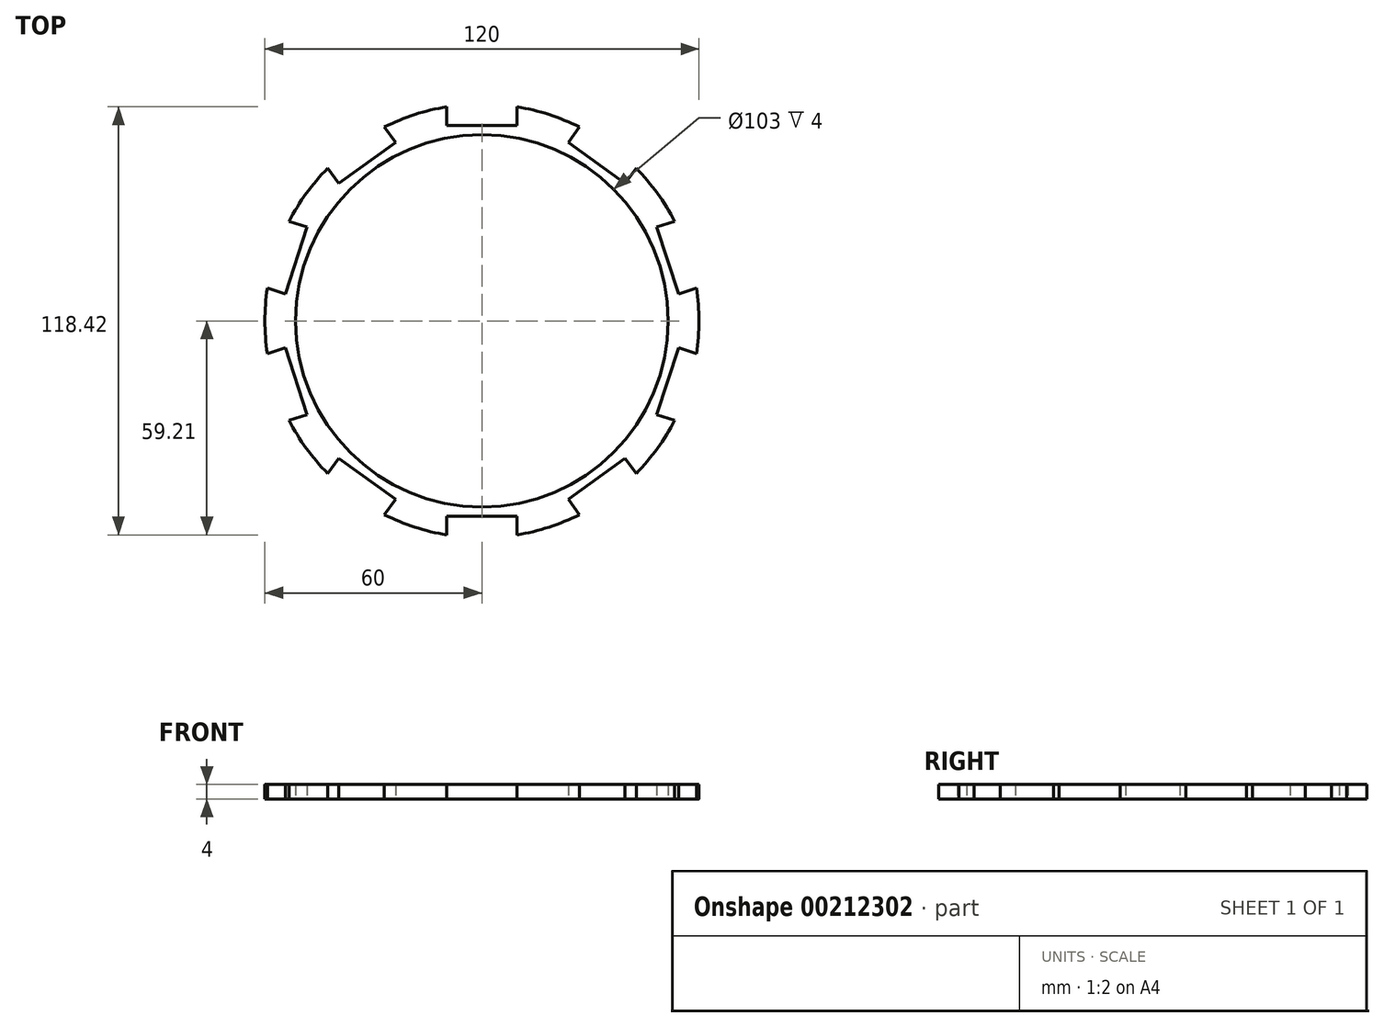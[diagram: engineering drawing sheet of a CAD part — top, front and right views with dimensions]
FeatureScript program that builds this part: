
annotation { "Feature Type Name" : "Feature", "Feature Type Description" : "" }
export const myFeature = defineFeature(function(context is Context, id is Id, definition is map)
    precondition{}
    {
        {
            var Q0;
            Q0=qCreatedBy(makeId("Top.planeOp"),FACE);
            var sketch = newSketch(context, id + "F0", { "sketchPlane" : qUnion([Q0])});
            skCircle(sketch, "E0", {"center": v(0, 0) * mm, "radius": 50 * mm});
            skLineSegment(sketch, "E1", {"start": v(0, 0) * mm, "end": v(0, -93.47) * mm, "construction": true});
            skPoint(sketch, "E2", {"position": v(0, -54) * mm});
            skPoint(sketch, "E3", {"position": v(0, -50) * mm});
            skLineSegment(sketch, "E4.bottom", {"start": v(9.7, -54) * mm, "end": v(-9.7, -54) * mm});
            skLineSegment(sketch, "E4.top", {"start": v(9.7, -73.4) * mm, "end": v(-9.7, -73.4) * mm});
            skLineSegment(sketch, "E4.left", {"start": v(9.7, -54) * mm, "end": v(9.7, -73.4) * mm});
            skLineSegment(sketch, "E4.right", {"start": v(-9.7, -54) * mm, "end": v(-9.7, -73.4) * mm});
            skLineSegment(sketch, "E5.1.0", {"start": v(39.59, -37.99) * mm, "end": v(23.9, -49.39) * mm});
            skLineSegment(sketch, "E5.1.1", {"start": v(23.9, -49.39) * mm, "end": v(35.3, -65.08) * mm});
            skLineSegment(sketch, "E5.1.2", {"start": v(51, -53.68) * mm, "end": v(35.3, -65.08) * mm});
            skLineSegment(sketch, "E5.1.3", {"start": v(39.59, -37.99) * mm, "end": v(51, -53.68) * mm});
            skLineSegment(sketch, "E5.2.0", {"start": v(54.35, -7.46) * mm, "end": v(48.36, -25.91) * mm});
            skLineSegment(sketch, "E5.2.1", {"start": v(48.36, -25.91) * mm, "end": v(66.81, -31.9) * mm});
            skLineSegment(sketch, "E5.2.2", {"start": v(72.8, -13.46) * mm, "end": v(66.81, -31.9) * mm});
            skLineSegment(sketch, "E5.2.3", {"start": v(54.35, -7.46) * mm, "end": v(72.8, -13.46) * mm});
            skLineSegment(sketch, "E5.3.0", {"start": v(48.36, 25.91) * mm, "end": v(54.35, 7.46) * mm});
            skLineSegment(sketch, "E5.3.1", {"start": v(54.35, 7.46) * mm, "end": v(72.8, 13.46) * mm});
            skLineSegment(sketch, "E5.3.2", {"start": v(66.81, 31.9) * mm, "end": v(72.8, 13.46) * mm});
            skLineSegment(sketch, "E5.3.3", {"start": v(48.36, 25.91) * mm, "end": v(66.81, 31.9) * mm});
            skLineSegment(sketch, "E5.4.0", {"start": v(23.9, 49.39) * mm, "end": v(39.59, 37.99) * mm});
            skLineSegment(sketch, "E5.4.1", {"start": v(39.59, 37.99) * mm, "end": v(51, 53.68) * mm});
            skLineSegment(sketch, "E5.4.2", {"start": v(35.3, 65.08) * mm, "end": v(51, 53.68) * mm});
            skLineSegment(sketch, "E5.4.3", {"start": v(23.9, 49.39) * mm, "end": v(35.3, 65.08) * mm});
            skLineSegment(sketch, "E5.5.0", {"start": v(-9.7, 54) * mm, "end": v(9.7, 54) * mm});
            skLineSegment(sketch, "E5.5.1", {"start": v(9.7, 54) * mm, "end": v(9.7, 73.4) * mm});
            skLineSegment(sketch, "E5.5.2", {"start": v(-9.7, 73.4) * mm, "end": v(9.7, 73.4) * mm});
            skLineSegment(sketch, "E5.5.3", {"start": v(-9.7, 54) * mm, "end": v(-9.7, 73.4) * mm});
            skLineSegment(sketch, "E5.6.0", {"start": v(-39.59, 37.99) * mm, "end": v(-23.9, 49.39) * mm});
            skLineSegment(sketch, "E5.6.1", {"start": v(-23.9, 49.39) * mm, "end": v(-35.3, 65.08) * mm});
            skLineSegment(sketch, "E5.6.2", {"start": v(-51, 53.68) * mm, "end": v(-35.3, 65.08) * mm});
            skLineSegment(sketch, "E5.6.3", {"start": v(-39.59, 37.99) * mm, "end": v(-51, 53.68) * mm});
            skLineSegment(sketch, "E5.7.0", {"start": v(-54.35, 7.46) * mm, "end": v(-48.36, 25.91) * mm});
            skLineSegment(sketch, "E5.7.1", {"start": v(-48.36, 25.91) * mm, "end": v(-66.81, 31.9) * mm});
            skLineSegment(sketch, "E5.7.2", {"start": v(-72.8, 13.46) * mm, "end": v(-66.81, 31.9) * mm});
            skLineSegment(sketch, "E5.7.3", {"start": v(-54.35, 7.46) * mm, "end": v(-72.8, 13.46) * mm});
            skLineSegment(sketch, "E5.8.0", {"start": v(-48.36, -25.91) * mm, "end": v(-54.35, -7.46) * mm});
            skLineSegment(sketch, "E5.8.1", {"start": v(-54.35, -7.46) * mm, "end": v(-72.8, -13.46) * mm});
            skLineSegment(sketch, "E5.8.2", {"start": v(-66.81, -31.9) * mm, "end": v(-72.8, -13.46) * mm});
            skLineSegment(sketch, "E5.8.3", {"start": v(-48.36, -25.91) * mm, "end": v(-66.81, -31.9) * mm});
            skLineSegment(sketch, "E5.9.0", {"start": v(-23.9, -49.39) * mm, "end": v(-39.59, -37.99) * mm});
            skLineSegment(sketch, "E5.9.1", {"start": v(-39.59, -37.99) * mm, "end": v(-51, -53.68) * mm});
            skLineSegment(sketch, "E5.9.2", {"start": v(-35.3, -65.08) * mm, "end": v(-51, -53.68) * mm});
            skLineSegment(sketch, "E5.9.3", {"start": v(-23.9, -49.39) * mm, "end": v(-35.3, -65.08) * mm});
            skSolve(sketch);
        }
        {
            var Q0;
            Q0=qCreatedBy(makeId("Top.planeOp"),FACE);
            var sketch = newSketch(context, id + "F1", { "sketchPlane" : qUnion([Q0])});
            skCircle(sketch, "E6", {"center": v(0, 0) * mm, "radius": 51.5 * mm});
            skCircle(sketch, "E7", {"center": v(0, 0) * mm, "radius": 60 * mm});
            skLineSegment(sketch, "E8.0", {"start": v(9.7, 54) * mm, "end": v(9.7, 73.4) * mm});
            skLineSegment(sketch, "E8.1", {"start": v(-9.7, 54) * mm, "end": v(-9.7, 73.4) * mm});
            skLineSegment(sketch, "E8.2", {"start": v(-9.7, 54) * mm, "end": v(9.7, 54) * mm});
            skLineSegment(sketch, "E8.3", {"start": v(-9.7, 73.4) * mm, "end": v(9.7, 73.4) * mm});
            skPoint(sketch, "E8.4", {"position": v(0, 54) * mm});
            skLineSegment(sketch, "E9.0", {"start": v(-23.9, 49.39) * mm, "end": v(-35.3, 65.08) * mm});
            skLineSegment(sketch, "E9.1", {"start": v(-39.59, 37.99) * mm, "end": v(-23.9, 49.39) * mm});
            skLineSegment(sketch, "E9.2", {"start": v(-39.59, 37.99) * mm, "end": v(-51, 53.68) * mm});
            skLineSegment(sketch, "E9.3", {"start": v(-51, 53.68) * mm, "end": v(-35.3, 65.08) * mm});
            skLineSegment(sketch, "E9.4", {"start": v(-48.36, 25.91) * mm, "end": v(-66.81, 31.9) * mm});
            skLineSegment(sketch, "E9.5", {"start": v(-54.35, 7.46) * mm, "end": v(-48.36, 25.91) * mm});
            skLineSegment(sketch, "E9.6", {"start": v(-72.8, 13.46) * mm, "end": v(-66.81, 31.9) * mm});
            skLineSegment(sketch, "E9.7", {"start": v(-54.35, 7.46) * mm, "end": v(-72.8, 13.46) * mm});
            skLineSegment(sketch, "E9.8", {"start": v(-54.35, -7.46) * mm, "end": v(-72.8, -13.46) * mm});
            skLineSegment(sketch, "E9.9", {"start": v(-48.36, -25.91) * mm, "end": v(-54.35, -7.46) * mm});
            skLineSegment(sketch, "E9.10", {"start": v(-66.81, -31.9) * mm, "end": v(-72.8, -13.46) * mm});
            skLineSegment(sketch, "E9.11", {"start": v(-48.36, -25.91) * mm, "end": v(-66.81, -31.9) * mm});
            skLineSegment(sketch, "E9.12", {"start": v(-39.59, -37.99) * mm, "end": v(-51, -53.68) * mm});
            skLineSegment(sketch, "E9.13", {"start": v(-23.9, -49.39) * mm, "end": v(-39.59, -37.99) * mm});
            skLineSegment(sketch, "E9.14", {"start": v(-23.9, -49.39) * mm, "end": v(-35.3, -65.08) * mm});
            skLineSegment(sketch, "E9.15", {"start": v(-35.3, -65.08) * mm, "end": v(-51, -53.68) * mm});
            skLineSegment(sketch, "E9.16", {"start": v(9.7, -54) * mm, "end": v(9.7, -73.4) * mm});
            skLineSegment(sketch, "E9.17", {"start": v(9.7, -54) * mm, "end": v(-9.7, -54) * mm});
            skLineSegment(sketch, "E9.18", {"start": v(-9.7, -54) * mm, "end": v(-9.7, -73.4) * mm});
            skLineSegment(sketch, "E9.19", {"start": v(9.7, -73.4) * mm, "end": v(-9.7, -73.4) * mm});
            skLineSegment(sketch, "E9.20", {"start": v(23.9, -49.39) * mm, "end": v(35.3, -65.08) * mm});
            skLineSegment(sketch, "E9.21", {"start": v(51, -53.68) * mm, "end": v(35.3, -65.08) * mm});
            skLineSegment(sketch, "E9.22", {"start": v(39.59, -37.99) * mm, "end": v(51, -53.68) * mm});
            skLineSegment(sketch, "E9.23", {"start": v(39.59, -37.99) * mm, "end": v(23.9, -49.39) * mm});
            skLineSegment(sketch, "E9.24", {"start": v(48.36, -25.91) * mm, "end": v(66.81, -31.9) * mm});
            skLineSegment(sketch, "E9.25", {"start": v(72.8, -13.46) * mm, "end": v(66.81, -31.9) * mm});
            skLineSegment(sketch, "E9.26", {"start": v(54.35, -7.46) * mm, "end": v(72.8, -13.46) * mm});
            skLineSegment(sketch, "E9.27", {"start": v(54.35, -7.46) * mm, "end": v(48.36, -25.91) * mm});
            skLineSegment(sketch, "E9.28", {"start": v(54.35, 7.46) * mm, "end": v(72.8, 13.46) * mm});
            skLineSegment(sketch, "E9.29", {"start": v(66.81, 31.9) * mm, "end": v(72.8, 13.46) * mm});
            skLineSegment(sketch, "E9.30", {"start": v(48.36, 25.91) * mm, "end": v(54.35, 7.46) * mm});
            skLineSegment(sketch, "E9.31", {"start": v(48.36, 25.91) * mm, "end": v(66.81, 31.9) * mm});
            skLineSegment(sketch, "E9.32", {"start": v(39.59, 37.99) * mm, "end": v(51, 53.68) * mm});
            skLineSegment(sketch, "E9.33", {"start": v(23.9, 49.39) * mm, "end": v(39.59, 37.99) * mm});
            skLineSegment(sketch, "E9.34", {"start": v(35.3, 65.08) * mm, "end": v(51, 53.68) * mm});
            skLineSegment(sketch, "E9.35", {"start": v(23.9, 49.39) * mm, "end": v(35.3, 65.08) * mm});
            skSolve(sketch);
        }
        {
            var Q0;
            Q0=makeQuery(id+"F1.imprint","IMPRINT",FACE,{"disambiguationData":[TD([[makeQuery(id+"F1.imprint","IMPRINT",EDGE,{"derivedFrom":sQuery(id+"F1.wireOp",EDGE,"E6")}),-1.0]])]});
            extrude(context, id + "F2", {"entities" : qUnion([Q0]), "depth" : 4 * mm});
        }
    });
